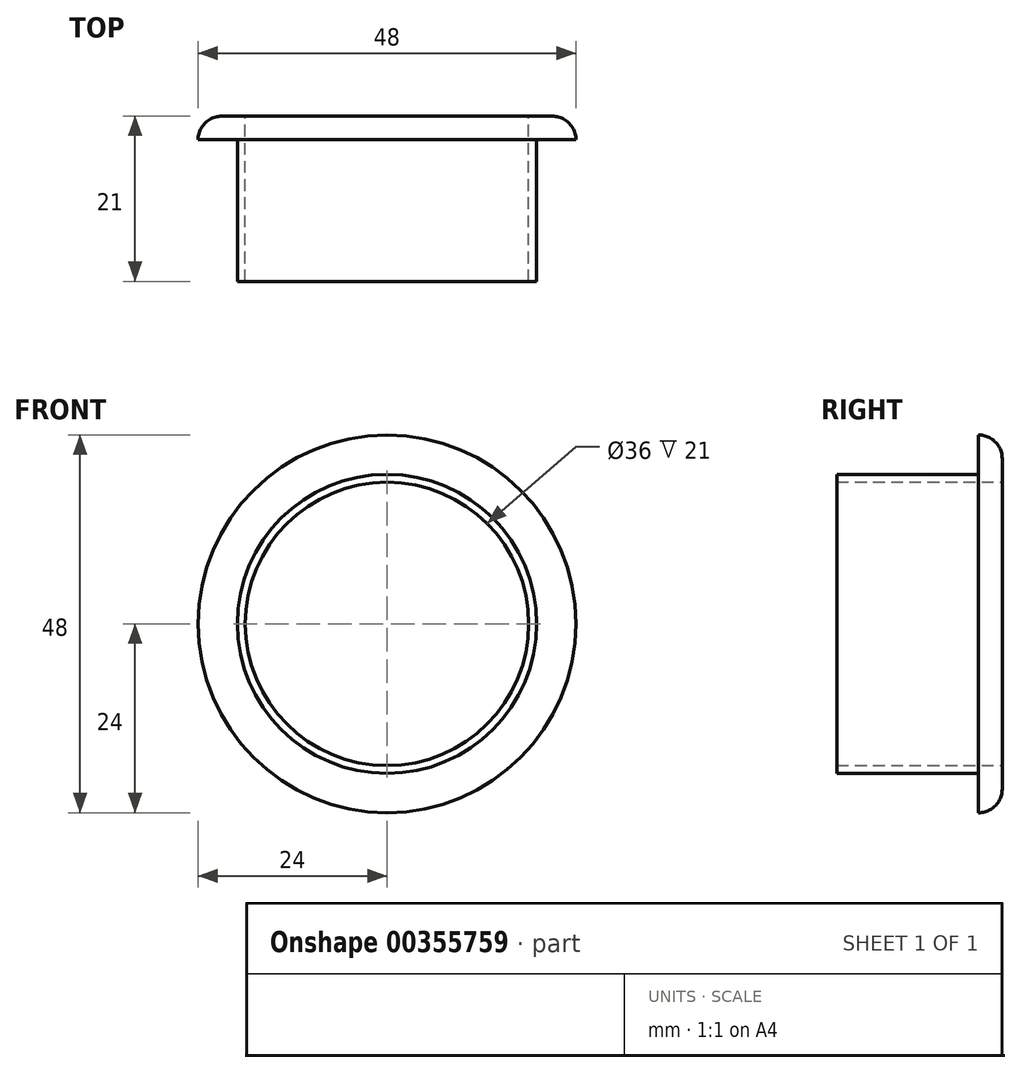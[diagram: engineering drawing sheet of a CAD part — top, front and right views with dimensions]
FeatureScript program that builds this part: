
annotation { "Feature Type Name" : "Feature", "Feature Type Description" : "" }
export const myFeature = defineFeature(function(context is Context, id is Id, definition is map)
    precondition{}
    {
        {
            var Q0;
            Q0=qCreatedBy(makeId("Front.planeOp"),FACE);
            var sketch = newSketch(context, id + "F0", { "sketchPlane" : qUnion([Q0])});
            skCircle(sketch, "E0", {"center": v(0, 0) * mm, "radius": 24 * mm});
            skSolve(sketch);
        }
        {
            var Q0;
            Q0 = qSketchRegion(id + "F0", true);
            extrude(context, id + "F1", {"entities" : qUnion([Q0]), "depth" : 3 * mm});
        }
        {
            var Q0;
            Q0=makeQuery(id+"F1.opExtrude","CAP_FACE",FACE,{"disambiguationData":[OSD([sQuery(id+"F0.wireOp",EDGE,"E0")])],"isStart":false});
            var sketch = newSketch(context, id + "F2", { "sketchPlane" : qUnion([Q0])});
            skCircle(sketch, "E1", {"center": v(0, 0) * mm, "radius": 19 * mm});
            skSolve(sketch);
        }
        {
            var Q0;
            Q0 = qSketchRegion(id + "F2", true);
            extrude(context, id + "F3", {"entities" : qUnion([Q0]), "operationType" : NewBodyOperationType.ADD, "depth" : 18 * mm});
        }
        {
            var Q0;
            Q0=makeQuery(id+"F1.opExtrude","CAP_FACE",FACE,{"disambiguationData":[OSD([sQuery(id+"F0.wireOp",EDGE,"E0")])],"isStart":true});
            var sketch = newSketch(context, id + "F4", { "sketchPlane" : qUnion([Q0])});
            skLineSegment(sketch, "E2", {"start": v(0, 0) * mm, "end": v(24, 0) * mm});
            skSolve(sketch);
        }
        {
            var Q0;
            Q0=sQuery(id+"F4.wireOp",VERTEX,"E2.start");
            var Q1;
            Q1=makeQuery(id+"F1.opExtrude","SWEPT_BODY",BODY,{"disambiguationData":[OSD([sQuery(id+"F0.wireOp",EDGE,"E0")])]});
            hole(context, id + "F5", {"style" : HoleStyle.SIMPLE, "endStyle" : HoleEndStyle.THROUGH, "holeDiameter" : 36 * mm, "tappedDepth" : 12 * mm, "tapClearance" : 3, "locations" : qUnion([Q0]), "scope" : qUnion([Q1])});
        }
        {
            var Q0;
            Q0=makeQuery(id+"F1.opExtrude","CAP_EDGE",EDGE,{"disambiguationData":[OSD([sQuery(id+"F0.wireOp",EDGE,"E0")])],"isStart":true});
            var Q1;
            Q1=makeQuery(id+"F5.hole-0.boolean.opBoolean","COPY",EDGE,{"derivedFrom":makeQuery(id+"F5.hole-0.opRevolve","SWEPT_EDGE",EDGE,{"disambiguationData":[OSD([sQuery(id+"F5.hole-0.sketch.wireOp",EDGE,"core_line_2"),sQuery(id+"F5.hole-0.sketch.wireOp",EDGE,"core_line_3")])]})});
            fillet(context, id + "F6", {"entities" : qUnion([Q0, Q1]), "radius" : 3 * mm, "tangentPropagation" : true, "allowEdgeOverflow" : false});
        }
    });
